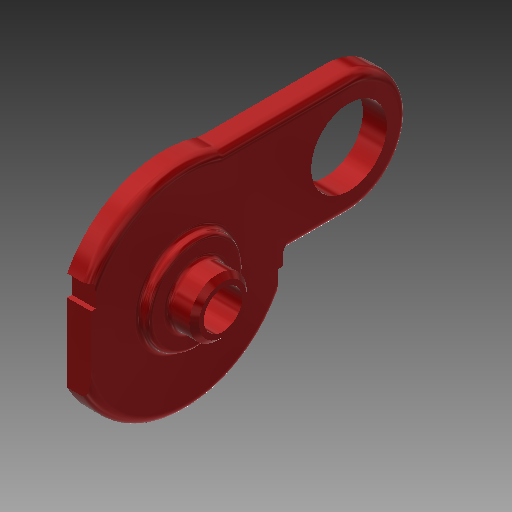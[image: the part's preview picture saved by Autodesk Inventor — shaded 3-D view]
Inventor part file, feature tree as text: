
AUTODESK INVENTOR PART (.ipt)
format: ipt  version: 2019 (Build 230136000, 136)  size: 412,160 bytes
history: native  units: mm
features: sketch x6, extrude x5, fillet x4, revolve x1
ambient origin geometry x8: Origin, YZ Plane, XZ Plane, XY Plane, X Axis, Y Axis, Z Axis, Center Point
bodies: Solid1 (feature_tree)
feature tree (16):
  revolve  "Revolution1"  [1 undecoded]
  extrude  "Extrusion1"  Depth=6.0mm
  extrude  "Extrusion2"  Depth=2.0mm
  extrude  "Extrusion3"  Depth=1.0mm
  extrude  "Extrusion4"  Depth=10.0mm
  fillet  "Fillet2"  [1 undecoded]
  fillet  "Fillet3"  Radius=40.0mm
  fillet  "Fillet4"  Radius=20.0mm
  extrude  "Extrusion5"  Depth=1.03mm
  fillet  "Fillet5"  Radius=10.0mm
  sketch  "Sketch1"  dims[d0=22.5mm d1=5.0mm]
  sketch  "Sketch2"  dims[d2=2.0mm d3=6.0mm]
  sketch  "Sketch3"  dims[d4=12.5mm d5=2.0mm]
  sketch  "Sketch4"  dims[d6=1.0mm d7=1.0mm]
  sketch  "Sketch5"  dims[d8=1.0mm d9=10.0mm d10=90.0deg d11=40.0mm d12=20.0mm]
  sketch  "Sketch6"  dims[d13=10.0mm d14=0.0mm d15=8.0mm d16=10.0mm d17=0.0mm d18=4.37mm d22=10.0mm d23=0.0mm d24=1.005mm d25=1.005mm d26=4.37mm d30=12.5mm d31=33.812825mm d32=8.723467mm d33=15.84mm d34=12.5mm d35=10.0mm d36=0.0mm d39=5.0mm d40=3.384658mm d41=2.033mm d42=1.0mm d43=5.0mm d45=1.25mm d46=1.25mm d47=12.5mm d48=18.0mm d49=1.745329mm d50=1.745329mm d51=1.745329mm d52=0.872665mm d53=1.745329mm d54=1.745329mm d55=1.745329mm d56=11.25mm d57=2.08mm d58=2.08mm d59=11.25mm d60=1.598436mm d61=1.592354mm d62=1.592354mm d63=0.799218mm d64=3.0mm d65=0.0mm d66=1.03mm]
note: 2 required parameter values undecoded (feature->parameter linkage not recoverable at this tier; creation-order binding heuristic only, values carry confidence <= 0.55)